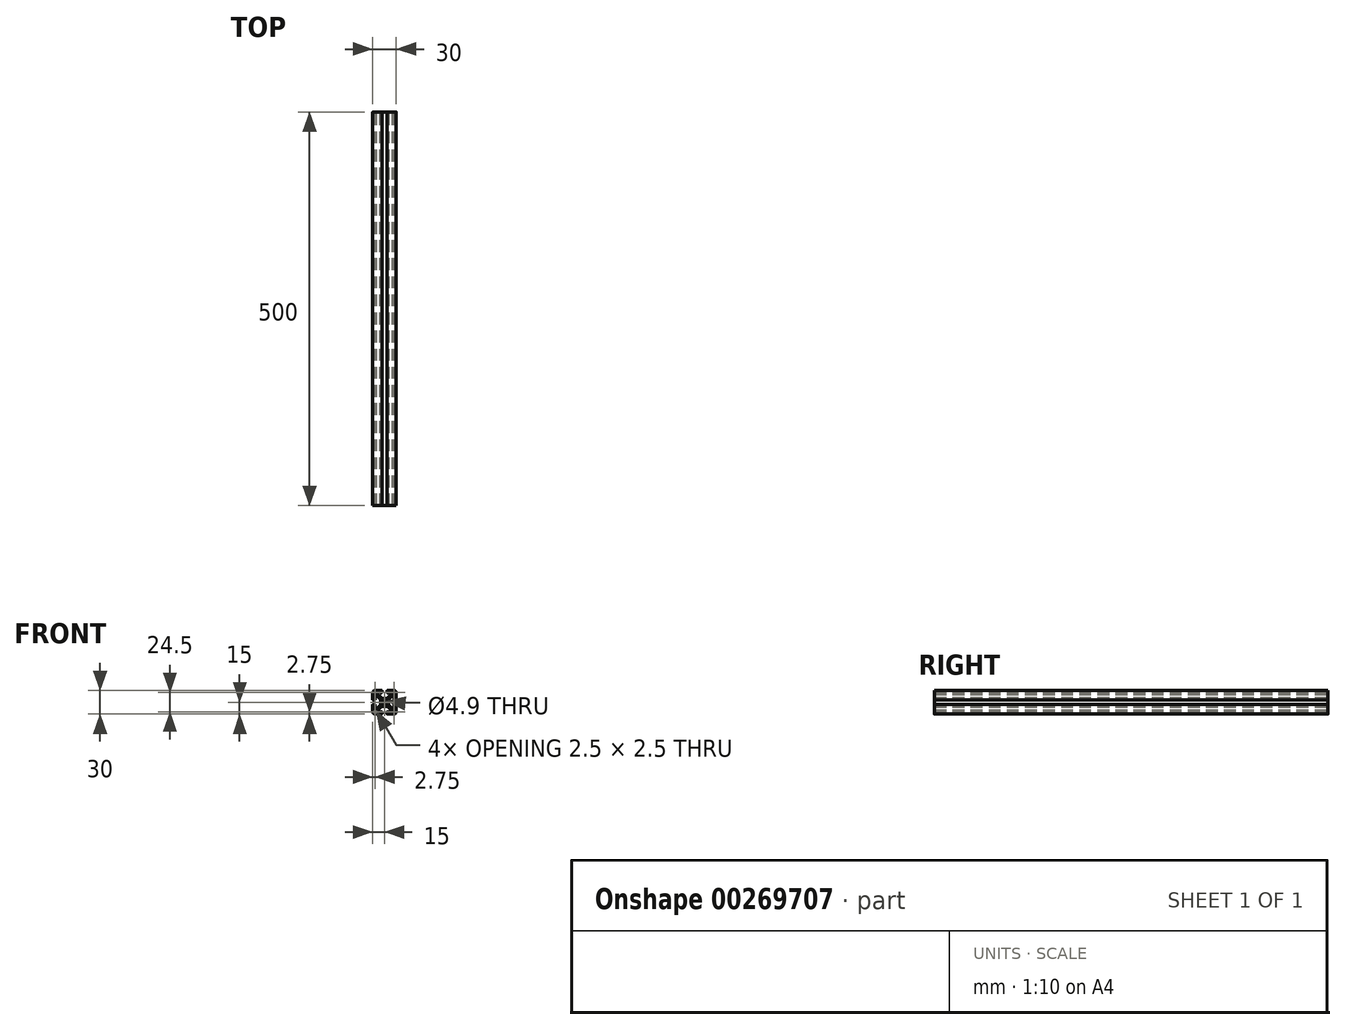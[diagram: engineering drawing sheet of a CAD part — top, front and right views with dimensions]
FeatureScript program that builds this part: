
annotation { "Feature Type Name" : "Feature", "Feature Type Description" : "" }
export const myFeature = defineFeature(function(context is Context, id is Id, definition is map)
    precondition{}
    {
        {
            var Q0;
            Q0=qCreatedBy(makeId("Front.planeOp"),FACE);
            var sketch = newSketch(context, id + "F0", { "sketchPlane" : qUnion([Q0])});
            skCircle(sketch, "E0", {"center": v(0, 0) * mm, "radius": 2.45 * mm});
            skLineSegment(sketch, "E1", {"start": v(-12, -15) * mm, "end": v(-3.5, -15) * mm});
            skLineSegment(sketch, "E2", {"start": v(-3, -14.5) * mm, "end": v(-3, -12.6) * mm});
            skLineSegment(sketch, "E3", {"start": v(-3.5, -12.1) * mm, "end": v(-5.4, -12.1) * mm});
            skLineSegment(sketch, "E4", {"start": v(-5.9, -12.6) * mm, "end": v(-5.9, -13) * mm});
            skLineSegment(sketch, "E5", {"start": v(-6.4, -13.5) * mm, "end": v(-9.5, -13.5) * mm});
            skLineSegment(sketch, "E6", {"start": v(-10, -13) * mm, "end": v(-10, -12.6) * mm});
            skLineSegment(sketch, "E7", {"start": v(-9.27, -10.82) * mm, "end": v(-4.28, -5.83) * mm});
            skLineSegment(sketch, "E8", {"start": v(-2.5, -5.1) * mm, "end": v(0, -5.1) * mm});
            skLineSegment(sketch, "E9", {"start": v(0, 0) * mm, "end": v(-15, -15) * mm, "construction": true});
            skLineSegment(sketch, "E10", {"start": v(0, -5.1) * mm, "end": v(0, -2.45) * mm});
            skLineSegment(sketch, "E11", {"start": v(-12.5, -13.5) * mm, "end": v(-11.5, -13.5) * mm});
            skLineSegment(sketch, "E12", {"start": v(-11, -13) * mm, "end": v(-11, -11.5) * mm});
            skPoint(sketch, "E13.visualSharp", {"position": v(-15, -15) * mm});
            skArc(sketch, "E13.filletArc", {"start": v(-15, -12) * mm, "mid": v(-14.12, -14.12) * mm, "end": v(-12, -15) * mm});
            skLineSegment(sketch, "E14", {"start": v(-13.5, -12.5) * mm, "end": v(-13.5, -11.5) * mm});
            skLineSegment(sketch, "E15", {"start": v(-13, -11) * mm, "end": v(-11.5, -11) * mm});
            skPoint(sketch, "E16.visualSharp", {"position": v(-13.5, -13.5) * mm});
            skArc(sketch, "E16.filletArc", {"start": v(-13.5, -12.5) * mm, "mid": v(-13.2, -13.2) * mm, "end": v(-12.5, -13.5) * mm});
            skPoint(sketch, "E17.visualSharp", {"position": v(-3, -15) * mm});
            skArc(sketch, "E17.filletArc", {"start": v(-3.5, -15) * mm, "mid": v(-3.15, -14.85) * mm, "end": v(-3, -14.5) * mm});
            skPoint(sketch, "E18.visualSharp", {"position": v(-3, -12.1) * mm});
            skArc(sketch, "E18.filletArc", {"start": v(-3, -12.6) * mm, "mid": v(-3.15, -12.25) * mm, "end": v(-3.5, -12.1) * mm});
            skPoint(sketch, "E19.visualSharp", {"position": v(-5.9, -12.1) * mm});
            skArc(sketch, "E19.filletArc", {"start": v(-5.4, -12.1) * mm, "mid": v(-5.75, -12.25) * mm, "end": v(-5.9, -12.6) * mm});
            skPoint(sketch, "E20.visualSharp", {"position": v(-5.9, -13.5) * mm});
            skArc(sketch, "E20.filletArc", {"start": v(-6.4, -13.5) * mm, "mid": v(-6.05, -13.35) * mm, "end": v(-5.9, -13) * mm});
            skPoint(sketch, "E21.visualSharp", {"position": v(-10, -13.5) * mm});
            skArc(sketch, "E21.filletArc", {"start": v(-10, -13) * mm, "mid": v(-9.85, -13.35) * mm, "end": v(-9.5, -13.5) * mm});
            skPoint(sketch, "E22.visualSharp", {"position": v(-10, -11.56) * mm});
            skArc(sketch, "E22.filletArc", {"start": v(-9.27, -10.82) * mm, "mid": v(-9.8, -11.63) * mm, "end": v(-10, -12.6) * mm});
            skPoint(sketch, "E23.visualSharp", {"position": v(-3.54, -5.1) * mm});
            skArc(sketch, "E23.filletArc", {"start": v(-2.5, -5.1) * mm, "mid": v(-3.47, -5.3) * mm, "end": v(-4.28, -5.83) * mm});
            skPoint(sketch, "E24.visualSharp", {"position": v(-13.5, -11) * mm});
            skArc(sketch, "E24.filletArc", {"start": v(-13, -11) * mm, "mid": v(-13.35, -11.15) * mm, "end": v(-13.5, -11.5) * mm});
            skPoint(sketch, "E25.visualSharp", {"position": v(-11, -11) * mm});
            skArc(sketch, "E25.filletArc", {"start": v(-11, -11.5) * mm, "mid": v(-11.15, -11.15) * mm, "end": v(-11.5, -11) * mm});
            skPoint(sketch, "E26.visualSharp", {"position": v(-11, -13.5) * mm});
            skArc(sketch, "E26.filletArc", {"start": v(-11.5, -13.5) * mm, "mid": v(-11.15, -13.35) * mm, "end": v(-11, -13) * mm});
            skLineSegment(sketch, "E27.MirrorCS", {"start": v(-5.1, 0) * mm, "end": v(-2.45, 0) * mm});
            skLineSegment(sketch, "E28.MirrorCS", {"start": v(-5.1, -2.5) * mm, "end": v(-5.1, 0) * mm});
            skArc(sketch, "E29.MirrorCS", {"start": v(-5.1, -2.5) * mm, "mid": v(-5.3, -3.47) * mm, "end": v(-5.83, -4.28) * mm});
            skLineSegment(sketch, "E30.MirrorCS", {"start": v(-10.82, -9.27) * mm, "end": v(-5.83, -4.28) * mm});
            skArc(sketch, "E31.MirrorCS", {"start": v(-10.82, -9.27) * mm, "mid": v(-11.63, -9.8) * mm, "end": v(-12.6, -10) * mm});
            skLineSegment(sketch, "E32.MirrorCS", {"start": v(-13, -10) * mm, "end": v(-12.6, -10) * mm});
            skArc(sketch, "E33.MirrorCS", {"start": v(-13, -10) * mm, "mid": v(-13.35, -9.85) * mm, "end": v(-13.5, -9.5) * mm});
            skLineSegment(sketch, "E34.MirrorCS", {"start": v(-13.5, -6.4) * mm, "end": v(-13.5, -9.5) * mm});
            skArc(sketch, "E35.MirrorCS", {"start": v(-13.5, -6.4) * mm, "mid": v(-13.35, -6.05) * mm, "end": v(-13, -5.9) * mm});
            skLineSegment(sketch, "E36.MirrorCS", {"start": v(-12.6, -5.9) * mm, "end": v(-13, -5.9) * mm});
            skArc(sketch, "E37.MirrorCS", {"start": v(-12.1, -5.4) * mm, "mid": v(-12.25, -5.75) * mm, "end": v(-12.6, -5.9) * mm});
            skLineSegment(sketch, "E38.MirrorCS", {"start": v(-12.1, -3.5) * mm, "end": v(-12.1, -5.4) * mm});
            skArc(sketch, "E39.MirrorCS", {"start": v(-12.6, -3) * mm, "mid": v(-12.25, -3.15) * mm, "end": v(-12.1, -3.5) * mm});
            skLineSegment(sketch, "E40.MirrorCS", {"start": v(-14.5, -3) * mm, "end": v(-12.6, -3) * mm});
            skArc(sketch, "E41.MirrorCS", {"start": v(-15, -3.5) * mm, "mid": v(-14.85, -3.15) * mm, "end": v(-14.5, -3) * mm});
            skLineSegment(sketch, "E42.MirrorCS", {"start": v(-15, -12) * mm, "end": v(-15, -3.5) * mm});
            skSolve(sketch);
        }
        {
            var Q0;
            Q0=makeQuery(id+"F0.imprint","IMPRINT",FACE,{"disambiguationData":[TD([[makeQuery(id+"F0.imprint","IMPRINT",EDGE,{"derivedFrom":sQuery(id+"F0.wireOp",EDGE,"E1")}),1.0]])]});
            extrude(context, id + "F1", {"entities" : qUnion([Q0]), "depth" : 500 * mm});
        }
        {
            var Q0;
            Q0=makeQuery(id+"F1.opExtrude","SWEPT_BODY",BODY,{"disambiguationData":[OSD([sQuery(id+"F0.wireOp",EDGE,"sQIJ9Odq-b0Rn-MLzu-FW2w-e5JDNjzKFSBt.top"),sQuery(id+"F0.wireOp",EDGE,"E0"),sQuery(id+"F0.wireOp",EDGE,"xx0pEBMj-jRSv-Lbnr-q3nJ-SJRiq3M36ffO"),sQuery(id+"F0.wireOp",EDGE,"HhF859K8-YMkQ-MNU6-Dy5O-0pLKfBP3kAkA"),sQuery(id+"F0.wireOp",EDGE,"wQfzR8yK-I87z-lzAA-hlza-ScneG80mE5Kx.bottom"),sQuery(id+"F0.wireOp",EDGE,"ee213793-e4f8-4bf9-8d0b-86dd017606e0.trimOffspring"),sQuery(id+"F0.wireOp",EDGE,"fb0eb2cd-e0d2-44c1-a6a0-7e2434b9a481.trimOffspring"),sQuery(id+"F0.wireOp",EDGE,"96611b80-2509-4977-8ee0-dc28bf1ca2f1.trimOffspring"),sQuery(id+"F0.wireOp",EDGE,"47d0e2af-7ef3-4dc7-b924-d975499c770c.0"),sQuery(id+"F0.wireOp",EDGE,"3deaeee3-6568-429b-9ed6-8287a86e409e.trimOffspring"),sQuery(id+"F0.wireOp",EDGE,"61d879a9-5d5b-4be7-a5b3-ab31b0cd3dda0.MirrorCS"),sQuery(id+"F0.wireOp",EDGE,"65f9af03-8806-4a07-9cf1-2c6853ba5d110.MirrorCS"),sQuery(id+"F0.wireOp",EDGE,"fc6a150f-2354-481d-a7f7-12314a61a3db0.MirrorCS"),sQuery(id+"F0.wireOp",EDGE,"995eec4f-409e-41a3-9068-15db16d9d5e60.MirrorCS"),sQuery(id+"F0.wireOp",EDGE,"2db985d2-f492-400f-9b34-f4d33f0a8f07.trimOffspring"),sQuery(id+"F0.wireOp",EDGE,"ce43019a-55f9-4d68-b8d0-760fdd826e6f.filletArc"),sQuery(id+"F0.wireOp",EDGE,"a8724986-b5a1-46ea-bf5f-6ffa4a1e30e5.filletArc"),sQuery(id+"F0.wireOp",EDGE,"39b65ee2-3660-40db-b114-eff3466c80ff.filletArc"),sQuery(id+"F0.wireOp",EDGE,"f029fb5f-1c6e-46a8-b066-c3309e76baca.filletArc"),sQuery(id+"F0.wireOp",EDGE,"fc5ba1e1-ee70-4e1b-a211-fe22d6c42d85.filletArc"),sQuery(id+"F0.wireOp",EDGE,"73bb0e17-f38b-4029-a0f5-6ff8f6ae8c53.filletArc"),sQuery(id+"F0.wireOp",EDGE,"f727079e-a9d2-4ab8-9029-b72e072e0ee8.filletArc"),sQuery(id+"F0.wireOp",EDGE,"b7393952-b5d3-4e23-be14-3641792003c9.filletArc"),sQuery(id+"F0.wireOp",EDGE,"6483bf9b-5064-456f-9927-321816dfa299.filletArc"),sQuery(id+"F0.wireOp",EDGE,"7e8644b9-a565-4610-a414-efdfb541d7c0.filletArc"),sQuery(id+"F0.wireOp",EDGE,"3c364d40-f7c2-43b0-9739-af362976f0dd.filletArc"),sQuery(id+"F0.wireOp",EDGE,"d72ed503-1d76-4e65-afc8-0e0d79af4015.filletArc"),sQuery(id+"F0.wireOp",EDGE,"da6769a0-2d57-4462-afa4-f72526fdd462.filletArc"),sQuery(id+"F0.wireOp",EDGE,"70a11764-b524-4b1b-b607-ab10562f5c3f.filletArc"),sQuery(id+"F0.wireOp",EDGE,"6924eca0-ff58-498d-b8bd-b16c23e8b2cb0.MirrorCS"),sQuery(id+"F0.wireOp",EDGE,"f35f10be-b5a2-41b0-8a69-31f264c1a07a0.MirrorCS"),sQuery(id+"F0.wireOp",EDGE,"94f3ad49-53e7-4236-97ce-5b07640e9eaa0.MirrorCS"),sQuery(id+"F0.wireOp",EDGE,"d720d22b-c961-47e7-bc98-783ad7491f650.MirrorCS"),sQuery(id+"F0.wireOp",EDGE,"ecf5aa19-f310-43ff-8f86-a85a364505830.MirrorCS"),sQuery(id+"F0.wireOp",EDGE,"d7d40bff-2da9-4aa4-bbee-0d4ccf0c007e0.MirrorCS"),sQuery(id+"F0.wireOp",EDGE,"93765ba6-aa2c-457b-89e4-11a6d18d483a0.MirrorCS"),sQuery(id+"F0.wireOp",EDGE,"3095ddbb-1c61-46f7-9eae-0dbeed0bd1520.MirrorCS"),sQuery(id+"F0.wireOp",EDGE,"3b4fba76-4828-4ad5-93f3-bf8473f690bd0.MirrorCS"),sQuery(id+"F0.wireOp",EDGE,"3ded5993-cf2c-4e72-8dc8-34aa7f0893480.MirrorCS"),sQuery(id+"F0.wireOp",EDGE,"06541b5c-ae92-41cb-9c0d-bf5c15adebfe0.MirrorCS"),sQuery(id+"F0.wireOp",EDGE,"03eeb4fa-4923-4edb-81bf-3a0c5e33ab1b0.MirrorCS"),sQuery(id+"F0.wireOp",EDGE,"64bc397e-93dd-4853-92eb-97f6d811ee280.MirrorCS"),sQuery(id+"F0.wireOp",EDGE,"f53d324d-155d-4a48-a95f-369b1fc3a1fa0.MirrorCS"),sQuery(id+"F0.wireOp",EDGE,"87bab2cf-f6c4-433c-aae3-60cc1768a2320.MirrorCS"),sQuery(id+"F0.wireOp",EDGE,"adf39f18-8477-4c84-8505-801bac79a5190.MirrorCS"),sQuery(id+"F0.wireOp",EDGE,"ecf04782-2938-4f9e-90a4-42a2d3213abb0.MirrorCS"),sQuery(id+"F0.wireOp",EDGE,"1ae9530a-3708-4acf-96bc-5eb43d106acc0.MirrorCS"),sQuery(id+"F0.wireOp",EDGE,"d705c9bc-ad35-4526-af5f-fe3209d504d70.MirrorCS"),sQuery(id+"F0.wireOp",EDGE,"6089a0e6-53cc-4c9e-8196-87fcd8f8d0e40.MirrorCS"),sQuery(id+"F0.wireOp",EDGE,"d10efab0-02c1-45cf-a92a-9f6f41025c4d0.MirrorCS"),sQuery(id+"F0.wireOp",EDGE,"62cceb8c-aae1-43db-8840-e491705a23ae0.MirrorCS"),sQuery(id+"F0.wireOp",EDGE,"75fbf65f-0392-42b3-a258-fbe8f2dbdabd0.MirrorCS"),sQuery(id+"F0.wireOp",EDGE,"bb8596a1-54b7-4a41-b693-59c539d133b00.MirrorCS"),sQuery(id+"F0.wireOp",EDGE,"52b521f5-73a9-4fdf-9f3a-9383cc9dab530.MirrorCS"),sQuery(id+"F0.wireOp",EDGE,"5cd4cdc2-9767-4388-9d50-3f43bb14d7240.MirrorCS"),sQuery(id+"F0.wireOp",EDGE,"84e0606f-2660-47d3-8066-1f6780e61d240.MirrorCS"),sQuery(id+"F0.wireOp",EDGE,"ewsHhfCt-k6IO-fkUO-DOpC-GD98c6aLlgUb"),sQuery(id+"F0.wireOp",EDGE,"WtLAROCM-aQHn-YKkG-DOua-fD37bnNfwTGD"),sQuery(id+"F0.wireOp",EDGE,"8777beac-d77c-45ca-af0e-820e461171390.MirrorCS"),sQuery(id+"F0.wireOp",EDGE,"8777beac-d77c-45ca-af0e-820e461171391.MirrorCS"),sQuery(id+"F0.wireOp",EDGE,"8777beac-d77c-45ca-af0e-820e461171393.MirrorCS"),sQuery(id+"F0.wireOp",EDGE,"8777beac-d77c-45ca-af0e-820e461171395.MirrorCS"),sQuery(id+"F0.wireOp",EDGE,"2eeeb882-eed5-4166-8e1e-a32fedb74f402.MirrorCS"),sQuery(id+"F0.wireOp",EDGE,"2eeeb882-eed5-4166-8e1e-a32fedb74f404.MirrorCS"),sQuery(id+"F0.wireOp",EDGE,"c7ab986a-4e71-4e94-875b-888b0b74b8760.MirrorCS"),sQuery(id+"F0.wireOp",EDGE,"30fd93c4-a74a-4645-b8f2-30fa4af6f5170.MirrorCS"),sQuery(id+"F0.wireOp",EDGE,"30fd93c4-a74a-4645-b8f2-30fa4af6f5171.MirrorCS"),sQuery(id+"F0.wireOp",EDGE,"30fd93c4-a74a-4645-b8f2-30fa4af6f5173.MirrorCS"),sQuery(id+"F0.wireOp",EDGE,"30fd93c4-a74a-4645-b8f2-30fa4af6f5174.MirrorCS"),sQuery(id+"F0.wireOp",EDGE,"30fd93c4-a74a-4645-b8f2-30fa4af6f5176.MirrorCS"),sQuery(id+"F0.wireOp",EDGE,"30fd93c4-a74a-4645-b8f2-30fa4af6f5177.MirrorCS"),sQuery(id+"F0.wireOp",EDGE,"30fd93c4-a74a-4645-b8f2-30fa4af6f5178.MirrorCS"),sQuery(id+"F0.wireOp",EDGE,"30fd93c4-a74a-4645-b8f2-30fa4af6f5179.MirrorCS"),sQuery(id+"F0.wireOp",EDGE,"c75a34bd-beff-4123-8e26-f2b4586136f20.MirrorCS"),sQuery(id+"F0.wireOp",EDGE,"d07f147f-3e59-4fec-a451-0a70723a730d0.MirrorCS"),sQuery(id+"F0.wireOp",EDGE,"25a2e1f4-fbdf-476f-b2df-d9d4e9416ce50.MirrorCS"),sQuery(id+"F0.wireOp",EDGE,"54c044ec-2a1f-477a-a750-c40de18a63860.MirrorCS"),sQuery(id+"F0.wireOp",EDGE,"e7b3a241-c0a6-4482-8933-493674b3ba2e0.MirrorCS"),sQuery(id+"F0.wireOp",EDGE,"564d2562-e668-4c5a-a657-de88a3b70ec20.MirrorCS"),sQuery(id+"F0.wireOp",EDGE,"NHzEeUZn-j6aY-zjJj-DU6j-r29A23V1wuZp"),sQuery(id+"F0.wireOp",EDGE,"euIQqrrk-acdu-msLV-AXC1-f6gACNh7W0Cw"),sQuery(id+"F0.wireOp",EDGE,"f90a4ee1-bbd4-4081-b289-277faebc6444.filletArc"),sQuery(id+"F0.wireOp",EDGE,"d731a9ce-1f9b-403d-a03f-e33f864c1e18.filletArc"),sQuery(id+"F0.wireOp",EDGE,"d0070ab0-448d-43b9-ae7c-de866852905e.filletArc"),sQuery(id+"F0.wireOp",EDGE,"63dcdacc-e304-4e1a-9721-d4ad0a47304f.filletArc"),sQuery(id+"F0.wireOp",EDGE,"35acc7aa-d704-43ea-868f-18a7ec3bdda70.MirrorCS"),sQuery(id+"F0.wireOp",EDGE,"fd040732-486b-4390-b425-ec4351d0e7e80.MirrorCS"),sQuery(id+"F0.wireOp",EDGE,"e578b67e-7911-4d93-92d3-7d22e9965f8e0.MirrorCS"),sQuery(id+"F0.wireOp",EDGE,"7a2807d8-86e2-4767-a200-7e81fd7f1f560.MirrorCS"),sQuery(id+"F0.wireOp",EDGE,"678a208d-c2a0-4aa2-b562-dc4c6234dfb40.MirrorCS"),sQuery(id+"F0.wireOp",EDGE,"f93236e3-4b4b-4808-aea5-9cdb7003f4050.MirrorCS"),sQuery(id+"F0.wireOp",EDGE,"0abef614-89f8-45e5-ac6e-1a178c9fc8b00.MirrorCS"),sQuery(id+"F0.wireOp",EDGE,"684fc782-96a6-47d3-a8c4-6e3182d5f3880.MirrorCS"),sQuery(id+"F0.wireOp",EDGE,"ae1c2d55-bc04-4e60-877a-dd5b8da22af00.MirrorCS"),sQuery(id+"F0.wireOp",EDGE,"662c4d57-50f4-4984-86b3-1351e2e6145b0.MirrorCS"),sQuery(id+"F0.wireOp",EDGE,"35bb1620-225b-454e-ac61-06da3b6371ea0.MirrorCS"),sQuery(id+"F0.wireOp",EDGE,"98add64f-431e-44f0-bccb-54f6e294647c0.MirrorCS"),sQuery(id+"F0.wireOp",EDGE,"13160950-3bda-40c9-b6f8-cbba89ccfef70.MirrorCS"),sQuery(id+"F0.wireOp",EDGE,"6be86dc8-a880-4c35-bcdf-8b3f5eee2cdd0.MirrorCS"),sQuery(id+"F0.wireOp",EDGE,"484c263f-cc48-46be-8847-f486bbebeede0.MirrorCS"),sQuery(id+"F0.wireOp",EDGE,"5f8588aa-2e83-4b97-b956-8e531a4eb46d0.MirrorCS"),sQuery(id+"F0.wireOp",EDGE,"2d822380-6e79-4d37-84ac-f398f3e25ab50.MirrorCS"),sQuery(id+"F0.wireOp",EDGE,"9ni5Pa1b-6vKT-ewqZ-4StL-2Qnwosqi4SmP"),sQuery(id+"F0.wireOp",EDGE,"3SnkwM6S-Ex2K-kpp2-J1OZ-N5tMk4ROZJVr"),sQuery(id+"F0.wireOp",EDGE,"02575252-a9dd-4ab6-bd93-705c5555701e0.MirrorCS"),sQuery(id+"F0.wireOp",EDGE,"101264cf-caa0-4dac-8bb7-761da2e68a4f0.MirrorCS"),sQuery(id+"F0.wireOp",EDGE,"66fab678-6442-4b16-833e-680aac1342370.MirrorCS"),sQuery(id+"F0.wireOp",EDGE,"d2d66b98-cc5c-436b-9ced-b73637c72f690.MirrorCS"),sQuery(id+"F0.wireOp",EDGE,"095b0e8a-5b2c-452e-882b-1944bbcbc7fe0.MirrorCS"),sQuery(id+"F0.wireOp",EDGE,"df691f2d-5f11-4f57-8a33-bca0a1592ec30.MirrorCS"),sQuery(id+"F0.wireOp",EDGE,"a2a9021a-c8e0-4c9d-9d7a-1de230806d980.MirrorCS"),sQuery(id+"F0.wireOp",EDGE,"ad83d616-585a-48a3-b278-d4401a45ed7e0.MirrorCS"),sQuery(id+"F0.wireOp",EDGE,"0347e20a-31d5-45e7-a402-947e340792340.MirrorCS"),sQuery(id+"F0.wireOp",EDGE,"5deaee7e-06ea-4911-bed0-68f2c0d7f7c50.MirrorCS"),sQuery(id+"F0.wireOp",EDGE,"zOQuU1W7-kDfO-8kRA-MtJh-F7DlEQ6mTgwY"),sQuery(id+"F0.wireOp",EDGE,"FsaTKIVf-019f-RWmk-kc5g-H0LFoSPPNp8z")])]});
            var Q1;
            Q1=qCreatedBy(makeId("Right.planeOp"),FACE);
            mirror(context, id + "F2", {"operationType" : NewBodyOperationType.ADD, "entities" : qUnion([Q0]), "mirrorPlane" : qUnion([Q1])});
        }
        {
            var Q0;
            Q0=makeQuery(id+"F1.opExtrude","SWEPT_BODY",BODY,{"disambiguationData":[OSD([sQuery(id+"F0.wireOp",EDGE,"E0"),sQuery(id+"F0.wireOp",EDGE,"E1"),sQuery(id+"F0.wireOp",EDGE,"E2"),sQuery(id+"F0.wireOp",EDGE,"E3"),sQuery(id+"F0.wireOp",EDGE,"E4"),sQuery(id+"F0.wireOp",EDGE,"E5"),sQuery(id+"F0.wireOp",EDGE,"E6"),sQuery(id+"F0.wireOp",EDGE,"E7"),sQuery(id+"F0.wireOp",EDGE,"E8"),sQuery(id+"F0.wireOp",EDGE,"E10"),sQuery(id+"F0.wireOp",EDGE,"E11"),sQuery(id+"F0.wireOp",EDGE,"E12"),sQuery(id+"F0.wireOp",EDGE,"E13.filletArc"),sQuery(id+"F0.wireOp",EDGE,"E14"),sQuery(id+"F0.wireOp",EDGE,"E15"),sQuery(id+"F0.wireOp",EDGE,"E16.filletArc"),sQuery(id+"F0.wireOp",EDGE,"E17.filletArc"),sQuery(id+"F0.wireOp",EDGE,"E18.filletArc"),sQuery(id+"F0.wireOp",EDGE,"E19.filletArc"),sQuery(id+"F0.wireOp",EDGE,"E20.filletArc"),sQuery(id+"F0.wireOp",EDGE,"E21.filletArc"),sQuery(id+"F0.wireOp",EDGE,"E22.filletArc"),sQuery(id+"F0.wireOp",EDGE,"E23.filletArc"),sQuery(id+"F0.wireOp",EDGE,"E24.filletArc"),sQuery(id+"F0.wireOp",EDGE,"E25.filletArc"),sQuery(id+"F0.wireOp",EDGE,"E26.filletArc"),sQuery(id+"F0.wireOp",EDGE,"E27.MirrorCS"),sQuery(id+"F0.wireOp",EDGE,"E28.MirrorCS"),sQuery(id+"F0.wireOp",EDGE,"E29.MirrorCS"),sQuery(id+"F0.wireOp",EDGE,"E30.MirrorCS"),sQuery(id+"F0.wireOp",EDGE,"E31.MirrorCS"),sQuery(id+"F0.wireOp",EDGE,"E32.MirrorCS"),sQuery(id+"F0.wireOp",EDGE,"E33.MirrorCS"),sQuery(id+"F0.wireOp",EDGE,"E34.MirrorCS"),sQuery(id+"F0.wireOp",EDGE,"E35.MirrorCS"),sQuery(id+"F0.wireOp",EDGE,"E36.MirrorCS"),sQuery(id+"F0.wireOp",EDGE,"E37.MirrorCS"),sQuery(id+"F0.wireOp",EDGE,"E38.MirrorCS"),sQuery(id+"F0.wireOp",EDGE,"E39.MirrorCS"),sQuery(id+"F0.wireOp",EDGE,"E40.MirrorCS"),sQuery(id+"F0.wireOp",EDGE,"E41.MirrorCS"),sQuery(id+"F0.wireOp",EDGE,"E42.MirrorCS")])]});
            var Q1;
            Q1=qCreatedBy(makeId("Top.planeOp"),FACE);
            mirror(context, id + "F3", {"operationType" : NewBodyOperationType.ADD, "entities" : qUnion([Q0]), "mirrorPlane" : qUnion([Q1])});
        }
    });
